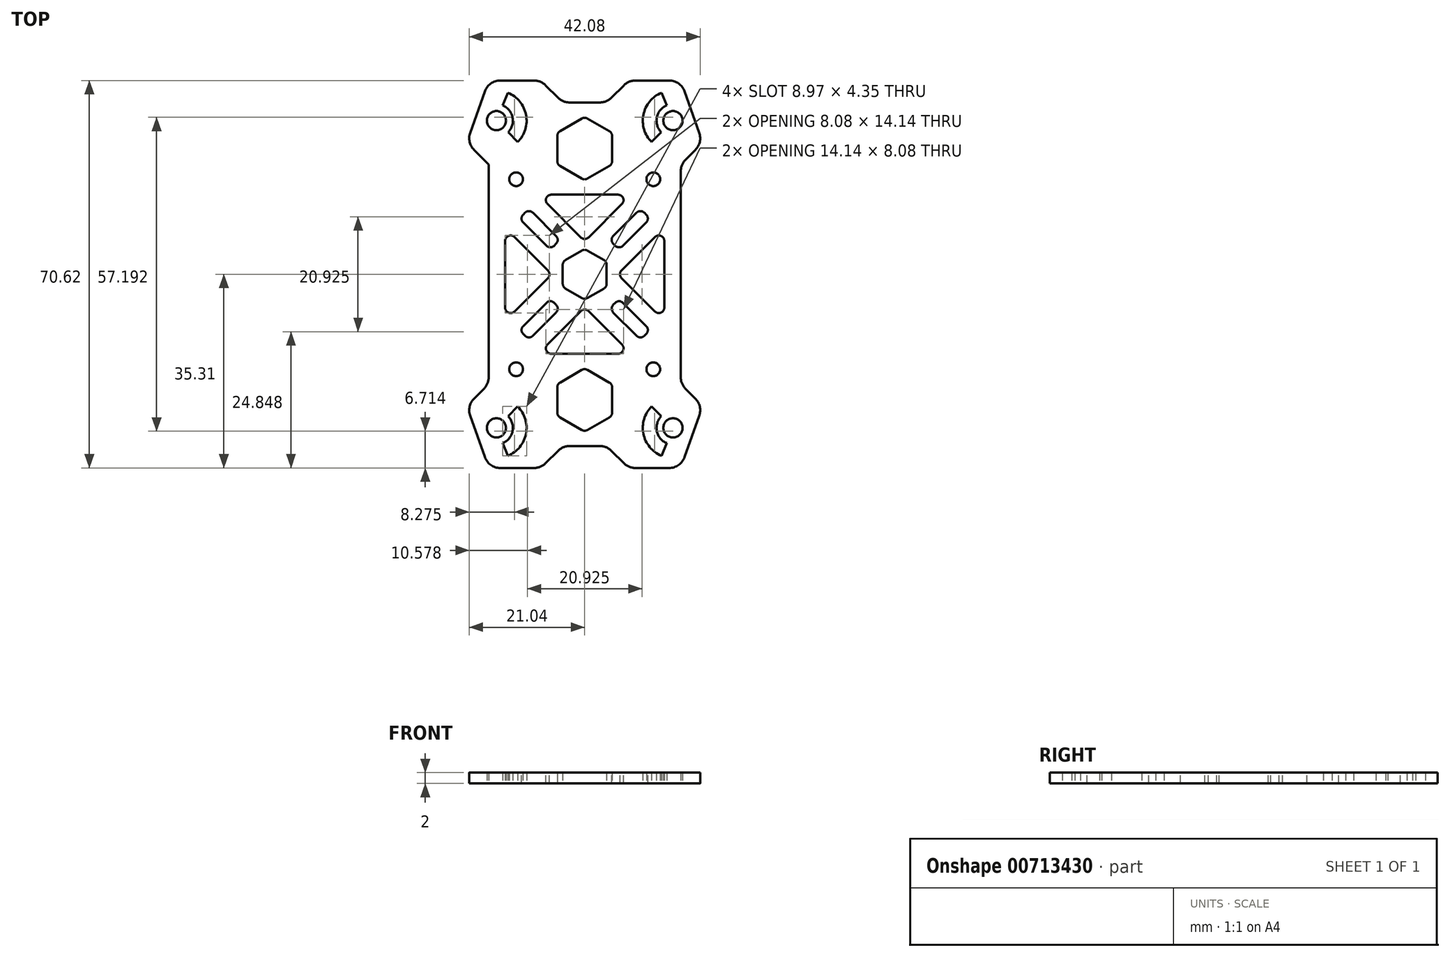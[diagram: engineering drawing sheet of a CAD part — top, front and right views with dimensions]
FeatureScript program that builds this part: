
annotation { "Feature Type Name" : "Feature", "Feature Type Description" : "" }
export const myFeature = defineFeature(function(context is Context, id is Id, definition is map)
    precondition{}
    {
        {
            var Q0;
            Q0=qCreatedBy(makeId("Top.planeOp"),FACE);
            var sketch = newSketch(context, id + "F0", { "sketchPlane" : qUnion([Q0])});
            skLineSegment(sketch, "E0.bottom", {"start": v(-10, 10) * mm, "end": v(10, 10) * mm, "construction": true});
            skLineSegment(sketch, "E0.top", {"start": v(-10, -10) * mm, "end": v(10, -10) * mm, "construction": true});
            skLineSegment(sketch, "E0.left", {"start": v(-10, 10) * mm, "end": v(-10, -10) * mm, "construction": true});
            skLineSegment(sketch, "E0.right", {"start": v(10, 10) * mm, "end": v(10, -10) * mm, "construction": true});
            skPoint(sketch, "E0.middle", {"position": v(0, 0) * mm});
            skCircle(sketch, "E1", {"center": v(-10, 10) * mm, "radius": 1.25 * mm});
            skCircle(sketch, "E2", {"center": v(10, 10) * mm, "radius": 1.25 * mm});
            skCircle(sketch, "E3", {"center": v(10, -10) * mm, "radius": 1.25 * mm});
            skCircle(sketch, "E4", {"center": v(-10, -10) * mm, "radius": 1.25 * mm});
            skLineSegment(sketch, "E5", {"start": v(-17.5, 20) * mm, "end": v(-17.5, -20) * mm});
            skLineSegment(sketch, "E6", {"start": v(-17.5, -20) * mm, "end": v(-21.5, -24) * mm});
            skLineSegment(sketch, "E7", {"start": v(-17.5, -35.31) * mm, "end": v(17.5, -35.31) * mm});
            skLineSegment(sketch, "E8", {"start": v(21.5, -24) * mm, "end": v(17.5, -20) * mm});
            skLineSegment(sketch, "E9", {"start": v(17.5, -20) * mm, "end": v(17.5, 20) * mm});
            skLineSegment(sketch, "E10", {"start": v(17.5, 20) * mm, "end": v(21.5, 24) * mm});
            skLineSegment(sketch, "E11", {"start": v(17.5, 35.31) * mm, "end": v(-17.5, 35.31) * mm});
            skLineSegment(sketch, "E12", {"start": v(-21.5, 24) * mm, "end": v(-17.5, 20) * mm});
            skLineSegment(sketch, "E13", {"start": v(-17.5, 0) * mm, "end": v(0, 0) * mm, "construction": true});
            skLineSegment(sketch, "E14", {"start": v(17.5, 0) * mm, "end": v(0, 0) * mm, "construction": true});
            skCircle(sketch, "E15", {"center": v(-16.09, 28) * mm, "radius": 1.75 * mm});
            skPoint(sketch, "E15.centerSnap0", {"position": v(-20.09, 28) * mm});
            skCircle(sketch, "E16", {"center": v(16.09, 28) * mm, "radius": 1.75 * mm});
            skPoint(sketch, "E16.centerSnap0", {"position": v(20.09, 28) * mm});
            skCircle(sketch, "E17", {"center": v(-16.09, -28) * mm, "radius": 1.75 * mm});
            skPoint(sketch, "E17.centerSnap0", {"position": v(-20.09, -28) * mm});
            skCircle(sketch, "E18", {"center": v(16.09, -28) * mm, "radius": 1.75 * mm});
            skPoint(sketch, "E18.centerSnap0", {"position": v(20.09, -28) * mm});
            skLineSegment(sketch, "E19", {"start": v(-16.09, 28) * mm, "end": v(-20.09, 28) * mm, "construction": true});
            skLineSegment(sketch, "E20", {"start": v(16.09, 28) * mm, "end": v(20.09, 28) * mm, "construction": true});
            skLineSegment(sketch, "E21", {"start": v(16.09, -28) * mm, "end": v(20.09, -28) * mm, "construction": true});
            skLineSegment(sketch, "E22", {"start": v(-16.09, -28) * mm, "end": v(-20.09, -28) * mm, "construction": true});
            skLineSegment(sketch, "E23", {"start": v(-21.5, 24) * mm, "end": v(-17.5, 35.31) * mm});
            skLineSegment(sketch, "E24", {"start": v(17.5, 35.31) * mm, "end": v(21.5, 24) * mm});
            skLineSegment(sketch, "E25", {"start": v(-17.5, -35.31) * mm, "end": v(-21.5, -24) * mm});
            skLineSegment(sketch, "E26", {"start": v(17.5, -35.31) * mm, "end": v(21.5, -24) * mm});
            skLineSegment(sketch, "E27", {"start": v(-16.09, 28) * mm, "end": v(-16.09, 20) * mm, "construction": true});
            skLineSegment(sketch, "E28", {"start": v(16.09, 20) * mm, "end": v(16.09, 28) * mm, "construction": true});
            skLineSegment(sketch, "E29", {"start": v(-16.09, -28) * mm, "end": v(-16.09, -20) * mm, "construction": true});
            skLineSegment(sketch, "E30", {"start": v(16.09, -28) * mm, "end": v(16.09, -20) * mm, "construction": true});
            skCircle(sketch, "E31.cCircle", {"center": v(0, 22.9) * mm, "radius": 5 * mm, "construction": true});
            skLineSegment(sketch, "E31.0", {"start": v(-5, 20.02) * mm, "end": v(-5, 25.8) * mm});
            skLineSegment(sketch, "E31.1", {"start": v(-5, 25.8) * mm, "end": v(0, 28.68) * mm});
            skLineSegment(sketch, "E31.2", {"start": v(0, 28.68) * mm, "end": v(5, 25.8) * mm});
            skLineSegment(sketch, "E31.3", {"start": v(5, 25.8) * mm, "end": v(5, 20.02) * mm});
            skLineSegment(sketch, "E31.4", {"start": v(5, 20.02) * mm, "end": v(0, 17.13) * mm});
            skLineSegment(sketch, "E31.5", {"start": v(0, 17.13) * mm, "end": v(-5, 20.02) * mm});
            skPoint(sketch, "E31.0.midPoint", {"position": v(-5, 22.9) * mm});
            skLineSegment(sketch, "E32", {"start": v(-11.92, 10.16) * mm, "end": v(-6.27, 4.5) * mm});
            skLineSegment(sketch, "E33", {"start": v(-6.27, 4.5) * mm, "end": v(-4.5, 6.27) * mm});
            skLineSegment(sketch, "E34", {"start": v(-4.5, 6.27) * mm, "end": v(-10.16, 11.92) * mm});
            skLineSegment(sketch, "E35", {"start": v(-10.16, 11.92) * mm, "end": v(-11.92, 10.16) * mm});
            skLineSegment(sketch, "E36.MirrorCS", {"start": v(4.5, 6.27) * mm, "end": v(10.16, 11.92) * mm});
            skLineSegment(sketch, "E37.MirrorCS", {"start": v(10.16, 11.92) * mm, "end": v(11.92, 10.16) * mm});
            skLineSegment(sketch, "E38.MirrorCS", {"start": v(11.92, 10.16) * mm, "end": v(6.27, 4.5) * mm});
            skLineSegment(sketch, "E39.MirrorCS", {"start": v(6.27, 4.5) * mm, "end": v(4.5, 6.27) * mm});
            skLineSegment(sketch, "E40.MirrorCS", {"start": v(11.92, -10.16) * mm, "end": v(6.27, -4.5) * mm});
            skLineSegment(sketch, "E41.MirrorCS", {"start": v(6.27, -4.5) * mm, "end": v(4.5, -6.27) * mm});
            skLineSegment(sketch, "E42.MirrorCS", {"start": v(4.5, -6.27) * mm, "end": v(10.16, -11.92) * mm});
            skLineSegment(sketch, "E43.MirrorCS", {"start": v(-6.27, -4.5) * mm, "end": v(-4.5, -6.27) * mm});
            skLineSegment(sketch, "E44.MirrorCS", {"start": v(-11.92, -10.16) * mm, "end": v(-6.27, -4.5) * mm});
            skLineSegment(sketch, "E45.MirrorCS", {"start": v(-4.5, -6.27) * mm, "end": v(-10.16, -11.92) * mm});
            skLineSegment(sketch, "E46.MirrorCS", {"start": v(-10.16, -11.92) * mm, "end": v(-11.92, -10.16) * mm});
            skLineSegment(sketch, "E47.MirrorCS", {"start": v(10.16, -11.92) * mm, "end": v(11.92, -10.16) * mm});
            skCircle(sketch, "E48", {"center": v(-12.5, 17.31) * mm, "radius": 1.25 * mm});
            skCircle(sketch, "E49", {"center": v(12.5, 17.31) * mm, "radius": 1.25 * mm});
            skCircle(sketch, "E50", {"center": v(-12.5, -17.31) * mm, "radius": 1.25 * mm});
            skCircle(sketch, "E51", {"center": v(12.5, -17.31) * mm, "radius": 1.25 * mm});
            skLineSegment(sketch, "E52", {"start": v(-12.5, 17.31) * mm, "end": v(-17.5, 17.31) * mm, "construction": true});
            skLineSegment(sketch, "E53", {"start": v(-12.5, 17.31) * mm, "end": v(-12.5, 35.31) * mm, "construction": true});
            skLineSegment(sketch, "E54", {"start": v(12.5, 17.31) * mm, "end": v(12.5, 35.31) * mm, "construction": true});
            skLineSegment(sketch, "E55", {"start": v(12.5, 17.31) * mm, "end": v(17.5, 17.31) * mm, "construction": true});
            skLineSegment(sketch, "E56", {"start": v(-12.5, -17.31) * mm, "end": v(-12.5, -35.31) * mm, "construction": true});
            skLineSegment(sketch, "E57", {"start": v(12.5, -17.31) * mm, "end": v(12.5, -35.31) * mm, "construction": true});
            skLineSegment(sketch, "E58", {"start": v(-12.5, -17.31) * mm, "end": v(-17.5, -17.31) * mm, "construction": true});
            skLineSegment(sketch, "E59", {"start": v(12.5, -17.31) * mm, "end": v(17.5, -17.31) * mm, "construction": true});
            skLineSegment(sketch, "E60", {"start": v(-6.01, 0) * mm, "end": v(-14.5, 8.49) * mm});
            skLineSegment(sketch, "E61", {"start": v(-14.5, 8.49) * mm, "end": v(-14.5, -8.49) * mm});
            skLineSegment(sketch, "E62", {"start": v(-14.5, -8.49) * mm, "end": v(-6.01, 0) * mm});
            skLineSegment(sketch, "E63.MirrorCS", {"start": v(6.01, 0) * mm, "end": v(14.5, 8.49) * mm});
            skLineSegment(sketch, "E64.MirrorCS", {"start": v(14.5, -8.49) * mm, "end": v(6.01, 0) * mm});
            skLineSegment(sketch, "E65.MirrorCS", {"start": v(14.5, 8.49) * mm, "end": v(14.5, -8.49) * mm});
            skLineSegment(sketch, "E66", {"start": v(-8.49, 14.5) * mm, "end": v(0, 6.01) * mm});
            skLineSegment(sketch, "E67", {"start": v(0, 6.01) * mm, "end": v(8.49, 14.5) * mm});
            skLineSegment(sketch, "E68", {"start": v(8.49, 14.5) * mm, "end": v(-8.49, 14.5) * mm});
            skLineSegment(sketch, "E69.MirrorCS", {"start": v(0, -6.01) * mm, "end": v(8.49, -14.5) * mm});
            skLineSegment(sketch, "E70.MirrorCS", {"start": v(-8.49, -14.5) * mm, "end": v(0, -6.01) * mm});
            skLineSegment(sketch, "E71.MirrorCS", {"start": v(8.49, -14.5) * mm, "end": v(-8.49, -14.5) * mm});
            skCircle(sketch, "E72.cCircle", {"center": v(0, 0) * mm, "radius": 4 * mm, "construction": true});
            skLineSegment(sketch, "E72.0", {"start": v(-4, -2.3) * mm, "end": v(-4, 2.3) * mm});
            skLineSegment(sketch, "E72.1", {"start": v(-4, 2.3) * mm, "end": v(0, 4.62) * mm});
            skLineSegment(sketch, "E72.2", {"start": v(0, 4.62) * mm, "end": v(4, 2.3) * mm});
            skLineSegment(sketch, "E72.3", {"start": v(4, 2.3) * mm, "end": v(4, -2.3) * mm});
            skLineSegment(sketch, "E72.4", {"start": v(4, -2.3) * mm, "end": v(0, -4.62) * mm});
            skLineSegment(sketch, "E72.5", {"start": v(0, -4.62) * mm, "end": v(-4, -2.3) * mm});
            skPoint(sketch, "E72.0.midPoint", {"position": v(-4, 0) * mm});
            skLineSegment(sketch, "E73.MirrorCS", {"start": v(-5, -25.8) * mm, "end": v(0, -28.68) * mm});
            skLineSegment(sketch, "E74.MirrorCS", {"start": v(0, -28.68) * mm, "end": v(5, -25.8) * mm});
            skLineSegment(sketch, "E75.MirrorCS", {"start": v(5, -20.02) * mm, "end": v(0, -17.13) * mm});
            skLineSegment(sketch, "E76.MirrorCS", {"start": v(5, -25.8) * mm, "end": v(5, -20.02) * mm});
            skLineSegment(sketch, "E77.MirrorCS", {"start": v(0, -17.13) * mm, "end": v(-5, -20.02) * mm});
            skLineSegment(sketch, "E78.MirrorCS", {"start": v(-5, -20.02) * mm, "end": v(-5, -25.8) * mm});
            skPoint(sketch, "E79.startSnap0", {"position": v(-18.09, 28) * mm});
            skLineSegment(sketch, "E80", {"start": v(-8, 35.31) * mm, "end": v(-4, 31.31) * mm});
            skLineSegment(sketch, "E81", {"start": v(-4, 31.31) * mm, "end": v(4, 31.31) * mm});
            skLineSegment(sketch, "E82", {"start": v(4, 31.31) * mm, "end": v(8, 35.31) * mm});
            skLineSegment(sketch, "E83", {"start": v(-8, 35.31) * mm, "end": v(-17.5, 35.31) * mm, "construction": true});
            skLineSegment(sketch, "E84", {"start": v(8, 35.31) * mm, "end": v(17.5, 35.31) * mm, "construction": true});
            skLineSegment(sketch, "E85.MirrorCS", {"start": v(-4, -31.31) * mm, "end": v(4, -31.31) * mm});
            skLineSegment(sketch, "E86.MirrorCS", {"start": v(-8, -35.31) * mm, "end": v(-4, -31.31) * mm});
            skLineSegment(sketch, "E87.MirrorCS", {"start": v(4, -31.31) * mm, "end": v(8, -35.31) * mm});
            skArc(sketch, "E88.converted", {"start": v(-13.96, 25.88) * mm, "mid": v(-13.14, 28.59) * mm, "end": v(-14.94, 30.77) * mm});
            skArc(sketch, "E89.converted", {"start": v(-12.2, 24.11) * mm, "mid": v(-10.7, 29.07) * mm, "end": v(-13.98, 33.08) * mm});
            skLineSegment(sketch, "E90", {"start": v(-13.96, 25.88) * mm, "end": v(-12.2, 24.11) * mm});
            skLineSegment(sketch, "E91", {"start": v(-14.94, 30.77) * mm, "end": v(-13.98, 33.08) * mm});
            skArc(sketch, "E92.MirrorCS", {"start": v(12.2, 24.11) * mm, "mid": v(10.7, 29.07) * mm, "end": v(13.98, 33.08) * mm});
            skLineSegment(sketch, "E93.MirrorCS", {"start": v(13.96, 25.88) * mm, "end": v(12.2, 24.11) * mm});
            skArc(sketch, "E94.MirrorCS", {"start": v(13.96, 25.88) * mm, "mid": v(13.14, 28.59) * mm, "end": v(14.94, 30.77) * mm});
            skLineSegment(sketch, "E95.MirrorCS", {"start": v(14.94, 30.77) * mm, "end": v(13.98, 33.08) * mm});
            skLineSegment(sketch, "E96.MirrorCS", {"start": v(14.94, -30.77) * mm, "end": v(13.98, -33.08) * mm});
            skArc(sketch, "E97.MirrorCS", {"start": v(13.96, -25.88) * mm, "mid": v(13.14, -28.59) * mm, "end": v(14.94, -30.77) * mm});
            skLineSegment(sketch, "E98.MirrorCS", {"start": v(13.96, -25.88) * mm, "end": v(12.2, -24.11) * mm});
            skArc(sketch, "E99.MirrorCS", {"start": v(12.2, -24.11) * mm, "mid": v(10.7, -29.07) * mm, "end": v(13.98, -33.08) * mm});
            skArc(sketch, "E100.MirrorCS", {"start": v(-12.2, -24.11) * mm, "mid": v(-10.7, -29.07) * mm, "end": v(-13.98, -33.08) * mm});
            skLineSegment(sketch, "E101.MirrorCS", {"start": v(-14.94, -30.77) * mm, "end": v(-13.98, -33.08) * mm});
            skArc(sketch, "E102.MirrorCS", {"start": v(-13.96, -25.88) * mm, "mid": v(-13.14, -28.59) * mm, "end": v(-14.94, -30.77) * mm});
            skLineSegment(sketch, "E103.MirrorCS", {"start": v(-13.96, -25.88) * mm, "end": v(-12.2, -24.11) * mm});
            skLineSegment(sketch, "E104", {"start": v(0, 28.68) * mm, "end": v(0, 31.31) * mm, "construction": true});
            skLineSegment(sketch, "E105", {"start": v(0, 17.13) * mm, "end": v(0, 14.5) * mm, "construction": true});
            skSolve(sketch);
        }
        {
            var Q0;
            Q0=makeQuery(id+"F0.imprint","IMPRINT",FACE,{"disambiguationData":[TD([[makeQuery(id+"F0.imprint","IMPRINT",EDGE,{"derivedFrom":sQuery(id+"F0.wireOp",EDGE,"E5")}),1.0]])]});
            extrude(context, id + "F1", {"entities" : qUnion([Q0]), "depth" : 2 * mm, "offsetDistance" : 25 * mm});
        }
        {
            var Q0;
            Q0=makeQuery(id+"F1.opExtrude","SWEPT_EDGE",EDGE,{"disambiguationData":[OSD([sQuery(id+"F0.wireOp",EDGE,"E6"),sQuery(id+"F0.wireOp",EDGE,"E25")])]});
            var Q1;
            Q1=makeQuery(id+"F1.opExtrude","SWEPT_EDGE",EDGE,{"disambiguationData":[OSD([sQuery(id+"F0.wireOp",EDGE,"E5"),sQuery(id+"F0.wireOp",EDGE,"E6")])]});
            var Q2;
            Q2=makeQuery(id+"F1.opExtrude","SWEPT_EDGE",EDGE,{"disambiguationData":[OSD([sQuery(id+"F0.wireOp",EDGE,"E7"),sQuery(id+"F0.wireOp",EDGE,"E25")])]});
            var Q3;
            Q3=makeQuery(id+"F1.opExtrude","SWEPT_EDGE",EDGE,{"disambiguationData":[OSD([sQuery(id+"F0.wireOp",EDGE,"E7"),sQuery(id+"F0.wireOp",EDGE,"E26")])]});
            var Q4;
            Q4=makeQuery(id+"F1.opExtrude","SWEPT_EDGE",EDGE,{"disambiguationData":[OSD([sQuery(id+"F0.wireOp",EDGE,"E8"),sQuery(id+"F0.wireOp",EDGE,"E26")])]});
            var Q5;
            Q5=makeQuery(id+"F1.opExtrude","SWEPT_EDGE",EDGE,{"disambiguationData":[OSD([sQuery(id+"F0.wireOp",EDGE,"E8"),sQuery(id+"F0.wireOp",EDGE,"E9")])]});
            var Q6;
            Q6=makeQuery(id+"F1.opExtrude","SWEPT_EDGE",EDGE,{"disambiguationData":[OSD([sQuery(id+"F0.wireOp",EDGE,"E9"),sQuery(id+"F0.wireOp",EDGE,"E10")])]});
            var Q7;
            Q7=makeQuery(id+"F1.opExtrude","SWEPT_EDGE",EDGE,{"disambiguationData":[OSD([sQuery(id+"F0.wireOp",EDGE,"E10"),sQuery(id+"F0.wireOp",EDGE,"E24")])]});
            var Q8;
            Q8=makeQuery(id+"F1.opExtrude","SWEPT_EDGE",EDGE,{"disambiguationData":[OSD([sQuery(id+"F0.wireOp",EDGE,"E11"),sQuery(id+"F0.wireOp",EDGE,"E24")])]});
            var Q9;
            Q9=makeQuery(id+"F1.opExtrude","SWEPT_EDGE",EDGE,{"disambiguationData":[OSD([sQuery(id+"F0.wireOp",EDGE,"E11"),sQuery(id+"F0.wireOp",EDGE,"E23")])]});
            var Q10;
            Q10=makeQuery(id+"F1.opExtrude","SWEPT_EDGE",EDGE,{"disambiguationData":[OSD([sQuery(id+"F0.wireOp",EDGE,"E12"),sQuery(id+"F0.wireOp",EDGE,"E23")])]});
            var Q11;
            Q11=makeQuery(id+"F1.opExtrude","SWEPT_EDGE",EDGE,{"disambiguationData":[OSD([sQuery(id+"F0.wireOp",EDGE,"E7"),sQuery(id+"F0.wireOp",EDGE,"E86.MirrorCS")])]});
            var Q12;
            Q12=makeQuery(id+"F1.opExtrude","SWEPT_EDGE",EDGE,{"disambiguationData":[OSD([sQuery(id+"F0.wireOp",EDGE,"E85.MirrorCS"),sQuery(id+"F0.wireOp",EDGE,"E86.MirrorCS")])]});
            var Q13;
            Q13=makeQuery(id+"F1.opExtrude","SWEPT_EDGE",EDGE,{"disambiguationData":[OSD([sQuery(id+"F0.wireOp",EDGE,"E85.MirrorCS"),sQuery(id+"F0.wireOp",EDGE,"E87.MirrorCS")])]});
            var Q14;
            Q14=makeQuery(id+"F1.opExtrude","SWEPT_EDGE",EDGE,{"disambiguationData":[OSD([sQuery(id+"F0.wireOp",EDGE,"E7"),sQuery(id+"F0.wireOp",EDGE,"E87.MirrorCS")])]});
            var Q15;
            Q15=makeQuery(id+"F1.opExtrude","SWEPT_EDGE",EDGE,{"disambiguationData":[OSD([sQuery(id+"F0.wireOp",EDGE,"E11"),sQuery(id+"F0.wireOp",EDGE,"E80")])]});
            var Q16;
            Q16=makeQuery(id+"F1.opExtrude","SWEPT_EDGE",EDGE,{"disambiguationData":[OSD([sQuery(id+"F0.wireOp",EDGE,"E80"),sQuery(id+"F0.wireOp",EDGE,"E81")])]});
            var Q17;
            Q17=makeQuery(id+"F1.opExtrude","SWEPT_EDGE",EDGE,{"disambiguationData":[OSD([sQuery(id+"F0.wireOp",EDGE,"E81"),sQuery(id+"F0.wireOp",EDGE,"E82")])]});
            var Q18;
            Q18=makeQuery(id+"F1.opExtrude","SWEPT_EDGE",EDGE,{"disambiguationData":[OSD([sQuery(id+"F0.wireOp",EDGE,"E11"),sQuery(id+"F0.wireOp",EDGE,"E82")])]});
            fillet(context, id + "F2", {"entities" : qUnion([Q0, Q1, Q2, Q3, Q4, Q5, Q6, Q7, Q8, Q9, Q10, Q11, Q12, Q13, Q14, Q15, Q16, Q17, Q18]), "radius" : 3 * mm, "tangentPropagation" : true, "allowEdgeOverflow" : false});
        }
        {
            var Q0;
            Q0=makeQuery(id+"F1.opExtrude","SWEPT_EDGE",EDGE,{"disambiguationData":[OSD([sQuery(id+"F0.wireOp",EDGE,"E34"),sQuery(id+"F0.wireOp",EDGE,"E35")])]});
            var Q1;
            Q1=makeQuery(id+"F1.opExtrude","SWEPT_EDGE",EDGE,{"disambiguationData":[OSD([sQuery(id+"F0.wireOp",EDGE,"E32"),sQuery(id+"F0.wireOp",EDGE,"E35")])]});
            var Q2;
            Q2=makeQuery(id+"F1.opExtrude","SWEPT_EDGE",EDGE,{"disambiguationData":[OSD([sQuery(id+"F0.wireOp",EDGE,"E33"),sQuery(id+"F0.wireOp",EDGE,"E34")])]});
            var Q3;
            Q3=makeQuery(id+"F1.opExtrude","SWEPT_EDGE",EDGE,{"disambiguationData":[OSD([sQuery(id+"F0.wireOp",EDGE,"E32"),sQuery(id+"F0.wireOp",EDGE,"E33")])]});
            var Q4;
            Q4=makeQuery(id+"F1.opExtrude","SWEPT_EDGE",EDGE,{"disambiguationData":[OSD([sQuery(id+"F0.wireOp",EDGE,"E36.MirrorCS"),sQuery(id+"F0.wireOp",EDGE,"E37.MirrorCS")])]});
            var Q5;
            Q5=makeQuery(id+"F1.opExtrude","SWEPT_EDGE",EDGE,{"disambiguationData":[OSD([sQuery(id+"F0.wireOp",EDGE,"E37.MirrorCS"),sQuery(id+"F0.wireOp",EDGE,"E38.MirrorCS")])]});
            var Q6;
            Q6=makeQuery(id+"F1.opExtrude","SWEPT_EDGE",EDGE,{"disambiguationData":[OSD([sQuery(id+"F0.wireOp",EDGE,"E38.MirrorCS"),sQuery(id+"F0.wireOp",EDGE,"E39.MirrorCS")])]});
            var Q7;
            Q7=makeQuery(id+"F1.opExtrude","SWEPT_EDGE",EDGE,{"disambiguationData":[OSD([sQuery(id+"F0.wireOp",EDGE,"E36.MirrorCS"),sQuery(id+"F0.wireOp",EDGE,"E39.MirrorCS")])]});
            var Q8;
            Q8=makeQuery(id+"F1.opExtrude","SWEPT_EDGE",EDGE,{"disambiguationData":[OSD([sQuery(id+"F0.wireOp",EDGE,"E44.MirrorCS"),sQuery(id+"F0.wireOp",EDGE,"E46.MirrorCS")])]});
            var Q9;
            Q9=makeQuery(id+"F1.opExtrude","SWEPT_EDGE",EDGE,{"disambiguationData":[OSD([sQuery(id+"F0.wireOp",EDGE,"E41.MirrorCS"),sQuery(id+"F0.wireOp",EDGE,"E42.MirrorCS")])]});
            var Q10;
            Q10=makeQuery(id+"F1.opExtrude","SWEPT_EDGE",EDGE,{"disambiguationData":[OSD([sQuery(id+"F0.wireOp",EDGE,"E43.MirrorCS"),sQuery(id+"F0.wireOp",EDGE,"E45.MirrorCS")])]});
            var Q11;
            Q11=makeQuery(id+"F1.opExtrude","SWEPT_EDGE",EDGE,{"disambiguationData":[OSD([sQuery(id+"F0.wireOp",EDGE,"E40.MirrorCS"),sQuery(id+"F0.wireOp",EDGE,"E47.MirrorCS")])]});
            var Q12;
            Q12=makeQuery(id+"F1.opExtrude","SWEPT_EDGE",EDGE,{"disambiguationData":[OSD([sQuery(id+"F0.wireOp",EDGE,"E42.MirrorCS"),sQuery(id+"F0.wireOp",EDGE,"E47.MirrorCS")])]});
            var Q13;
            Q13=makeQuery(id+"F1.opExtrude","SWEPT_EDGE",EDGE,{"disambiguationData":[OSD([sQuery(id+"F0.wireOp",EDGE,"E45.MirrorCS"),sQuery(id+"F0.wireOp",EDGE,"E46.MirrorCS")])]});
            var Q14;
            Q14=makeQuery(id+"F1.opExtrude","SWEPT_EDGE",EDGE,{"disambiguationData":[OSD([sQuery(id+"F0.wireOp",EDGE,"E43.MirrorCS"),sQuery(id+"F0.wireOp",EDGE,"E44.MirrorCS")])]});
            var Q15;
            Q15=makeQuery(id+"F1.opExtrude","SWEPT_EDGE",EDGE,{"disambiguationData":[OSD([sQuery(id+"F0.wireOp",EDGE,"E40.MirrorCS"),sQuery(id+"F0.wireOp",EDGE,"E41.MirrorCS")])]});
            var Q16;
            Q16=makeQuery(id+"F1.opExtrude","SWEPT_EDGE",EDGE,{"disambiguationData":[OSD([sQuery(id+"F0.wireOp",EDGE,"532293ea-ac90-4155-ae0c-07403808c71e.0"),sQuery(id+"F0.wireOp",EDGE,"532293ea-ac90-4155-ae0c-07403808c71e.5")])]});
            var Q17;
            Q17=makeQuery(id+"F1.opExtrude","SWEPT_EDGE",EDGE,{"disambiguationData":[OSD([sQuery(id+"F0.wireOp",EDGE,"532293ea-ac90-4155-ae0c-07403808c71e.4"),sQuery(id+"F0.wireOp",EDGE,"532293ea-ac90-4155-ae0c-07403808c71e.5")])]});
            var Q18;
            Q18=makeQuery(id+"F1.opExtrude","SWEPT_EDGE",EDGE,{"disambiguationData":[OSD([sQuery(id+"F0.wireOp",EDGE,"532293ea-ac90-4155-ae0c-07403808c71e.3"),sQuery(id+"F0.wireOp",EDGE,"532293ea-ac90-4155-ae0c-07403808c71e.4")])]});
            var Q19;
            Q19=makeQuery(id+"F1.opExtrude","SWEPT_EDGE",EDGE,{"disambiguationData":[OSD([sQuery(id+"F0.wireOp",EDGE,"532293ea-ac90-4155-ae0c-07403808c71e.2"),sQuery(id+"F0.wireOp",EDGE,"532293ea-ac90-4155-ae0c-07403808c71e.3")])]});
            var Q20;
            Q20=makeQuery(id+"F1.opExtrude","SWEPT_EDGE",EDGE,{"disambiguationData":[OSD([sQuery(id+"F0.wireOp",EDGE,"532293ea-ac90-4155-ae0c-07403808c71e.1"),sQuery(id+"F0.wireOp",EDGE,"532293ea-ac90-4155-ae0c-07403808c71e.2")])]});
            var Q21;
            Q21=makeQuery(id+"F1.opExtrude","SWEPT_EDGE",EDGE,{"disambiguationData":[OSD([sQuery(id+"F0.wireOp",EDGE,"532293ea-ac90-4155-ae0c-07403808c71e.0"),sQuery(id+"F0.wireOp",EDGE,"532293ea-ac90-4155-ae0c-07403808c71e.1")])]});
            var Q22;
            Q22=makeQuery(id+"F1.opExtrude","SWEPT_EDGE",EDGE,{"disambiguationData":[OSD([sQuery(id+"F0.wireOp",EDGE,"ea0782d6-4afa-4406-878f-a4188b14e591.4"),sQuery(id+"F0.wireOp",EDGE,"ea0782d6-4afa-4406-878f-a4188b14e591.5")])]});
            var Q23;
            Q23=makeQuery(id+"F1.opExtrude","SWEPT_EDGE",EDGE,{"disambiguationData":[OSD([sQuery(id+"F0.wireOp",EDGE,"ea0782d6-4afa-4406-878f-a4188b14e591.0"),sQuery(id+"F0.wireOp",EDGE,"ea0782d6-4afa-4406-878f-a4188b14e591.5")])]});
            var Q24;
            Q24=makeQuery(id+"F1.opExtrude","SWEPT_EDGE",EDGE,{"disambiguationData":[OSD([sQuery(id+"F0.wireOp",EDGE,"ea0782d6-4afa-4406-878f-a4188b14e591.0"),sQuery(id+"F0.wireOp",EDGE,"ea0782d6-4afa-4406-878f-a4188b14e591.1")])]});
            var Q25;
            Q25=makeQuery(id+"F1.opExtrude","SWEPT_EDGE",EDGE,{"disambiguationData":[OSD([sQuery(id+"F0.wireOp",EDGE,"ea0782d6-4afa-4406-878f-a4188b14e591.1"),sQuery(id+"F0.wireOp",EDGE,"ea0782d6-4afa-4406-878f-a4188b14e591.2")])]});
            var Q26;
            Q26=makeQuery(id+"F1.opExtrude","SWEPT_EDGE",EDGE,{"disambiguationData":[OSD([sQuery(id+"F0.wireOp",EDGE,"ea0782d6-4afa-4406-878f-a4188b14e591.2"),sQuery(id+"F0.wireOp",EDGE,"ea0782d6-4afa-4406-878f-a4188b14e591.3")])]});
            var Q27;
            Q27=makeQuery(id+"F1.opExtrude","SWEPT_EDGE",EDGE,{"disambiguationData":[OSD([sQuery(id+"F0.wireOp",EDGE,"ea0782d6-4afa-4406-878f-a4188b14e591.3"),sQuery(id+"F0.wireOp",EDGE,"ea0782d6-4afa-4406-878f-a4188b14e591.4")])]});
            var Q28;
            Q28=makeQuery(id+"F1.opExtrude","SWEPT_EDGE",EDGE,{"disambiguationData":[OSD([sQuery(id+"F0.wireOp",EDGE,"E31.3"),sQuery(id+"F0.wireOp",EDGE,"E31.4")])]});
            var Q29;
            Q29=makeQuery(id+"F1.opExtrude","SWEPT_EDGE",EDGE,{"disambiguationData":[OSD([sQuery(id+"F0.wireOp",EDGE,"E31.2"),sQuery(id+"F0.wireOp",EDGE,"E31.3")])]});
            var Q30;
            Q30=makeQuery(id+"F1.opExtrude","SWEPT_EDGE",EDGE,{"disambiguationData":[OSD([sQuery(id+"F0.wireOp",EDGE,"E31.1"),sQuery(id+"F0.wireOp",EDGE,"E31.2")])]});
            var Q31;
            Q31=makeQuery(id+"F1.opExtrude","SWEPT_EDGE",EDGE,{"disambiguationData":[OSD([sQuery(id+"F0.wireOp",EDGE,"E31.0"),sQuery(id+"F0.wireOp",EDGE,"E31.1")])]});
            var Q32;
            Q32=makeQuery(id+"F1.opExtrude","SWEPT_EDGE",EDGE,{"disambiguationData":[OSD([sQuery(id+"F0.wireOp",EDGE,"E31.0"),sQuery(id+"F0.wireOp",EDGE,"E31.5")])]});
            var Q33;
            Q33=makeQuery(id+"F1.opExtrude","SWEPT_EDGE",EDGE,{"disambiguationData":[OSD([sQuery(id+"F0.wireOp",EDGE,"E31.4"),sQuery(id+"F0.wireOp",EDGE,"E31.5")])]});
            var Q34;
            Q34=makeQuery(id+"F1.opExtrude","SWEPT_EDGE",EDGE,{"disambiguationData":[OSD([sQuery(id+"F0.wireOp",EDGE,"E69.MirrorCS"),sQuery(id+"F0.wireOp",EDGE,"E71.MirrorCS")])]});
            var Q35;
            Q35=makeQuery(id+"F1.opExtrude","SWEPT_EDGE",EDGE,{"disambiguationData":[OSD([sQuery(id+"F0.wireOp",EDGE,"E70.MirrorCS"),sQuery(id+"F0.wireOp",EDGE,"E71.MirrorCS")])]});
            var Q36;
            Q36=makeQuery(id+"F1.opExtrude","SWEPT_EDGE",EDGE,{"disambiguationData":[OSD([sQuery(id+"F0.wireOp",EDGE,"E69.MirrorCS"),sQuery(id+"F0.wireOp",EDGE,"E70.MirrorCS")])]});
            var Q37;
            Q37=makeQuery(id+"F1.opExtrude","SWEPT_EDGE",EDGE,{"disambiguationData":[OSD([sQuery(id+"F0.wireOp",EDGE,"E66"),sQuery(id+"F0.wireOp",EDGE,"E67")])]});
            var Q38;
            Q38=makeQuery(id+"F1.opExtrude","SWEPT_EDGE",EDGE,{"disambiguationData":[OSD([sQuery(id+"F0.wireOp",EDGE,"E67"),sQuery(id+"F0.wireOp",EDGE,"E68")])]});
            var Q39;
            Q39=makeQuery(id+"F1.opExtrude","SWEPT_EDGE",EDGE,{"disambiguationData":[OSD([sQuery(id+"F0.wireOp",EDGE,"E66"),sQuery(id+"F0.wireOp",EDGE,"E68")])]});
            var Q40;
            Q40=makeQuery(id+"F1.opExtrude","SWEPT_EDGE",EDGE,{"disambiguationData":[OSD([sQuery(id+"F0.wireOp",EDGE,"E60"),sQuery(id+"F0.wireOp",EDGE,"E62")])]});
            var Q41;
            Q41=makeQuery(id+"F1.opExtrude","SWEPT_EDGE",EDGE,{"disambiguationData":[OSD([sQuery(id+"F0.wireOp",EDGE,"E60"),sQuery(id+"F0.wireOp",EDGE,"E61")])]});
            var Q42;
            Q42=makeQuery(id+"F1.opExtrude","SWEPT_EDGE",EDGE,{"disambiguationData":[OSD([sQuery(id+"F0.wireOp",EDGE,"E61"),sQuery(id+"F0.wireOp",EDGE,"E62")])]});
            var Q43;
            Q43=makeQuery(id+"F1.opExtrude","SWEPT_EDGE",EDGE,{"disambiguationData":[OSD([sQuery(id+"F0.wireOp",EDGE,"E63.MirrorCS"),sQuery(id+"F0.wireOp",EDGE,"E65.MirrorCS")])]});
            var Q44;
            Q44=makeQuery(id+"F1.opExtrude","SWEPT_EDGE",EDGE,{"disambiguationData":[OSD([sQuery(id+"F0.wireOp",EDGE,"E63.MirrorCS"),sQuery(id+"F0.wireOp",EDGE,"E64.MirrorCS")])]});
            var Q45;
            Q45=makeQuery(id+"F1.opExtrude","SWEPT_EDGE",EDGE,{"disambiguationData":[OSD([sQuery(id+"F0.wireOp",EDGE,"E64.MirrorCS"),sQuery(id+"F0.wireOp",EDGE,"E65.MirrorCS")])]});
            var Q46;
            Q46=makeQuery(id+"F1.opExtrude","SWEPT_EDGE",EDGE,{"disambiguationData":[OSD([sQuery(id+"F0.wireOp",EDGE,"E77.MirrorCS"),sQuery(id+"F0.wireOp",EDGE,"E78.MirrorCS")])]});
            var Q47;
            Q47=makeQuery(id+"F1.opExtrude","SWEPT_EDGE",EDGE,{"disambiguationData":[OSD([sQuery(id+"F0.wireOp",EDGE,"E75.MirrorCS"),sQuery(id+"F0.wireOp",EDGE,"E77.MirrorCS")])]});
            var Q48;
            Q48=makeQuery(id+"F1.opExtrude","SWEPT_EDGE",EDGE,{"disambiguationData":[OSD([sQuery(id+"F0.wireOp",EDGE,"E75.MirrorCS"),sQuery(id+"F0.wireOp",EDGE,"E76.MirrorCS")])]});
            var Q49;
            Q49=makeQuery(id+"F1.opExtrude","SWEPT_EDGE",EDGE,{"disambiguationData":[OSD([sQuery(id+"F0.wireOp",EDGE,"E74.MirrorCS"),sQuery(id+"F0.wireOp",EDGE,"E76.MirrorCS")])]});
            var Q50;
            Q50=makeQuery(id+"F1.opExtrude","SWEPT_EDGE",EDGE,{"disambiguationData":[OSD([sQuery(id+"F0.wireOp",EDGE,"E73.MirrorCS"),sQuery(id+"F0.wireOp",EDGE,"E74.MirrorCS")])]});
            var Q51;
            Q51=makeQuery(id+"F1.opExtrude","SWEPT_EDGE",EDGE,{"disambiguationData":[OSD([sQuery(id+"F0.wireOp",EDGE,"E73.MirrorCS"),sQuery(id+"F0.wireOp",EDGE,"E78.MirrorCS")])]});
            var Q52;
            Q52=makeQuery(id+"F1.opExtrude","SWEPT_EDGE",EDGE,{"disambiguationData":[OSD([sQuery(id+"F0.wireOp",EDGE,"E72.2"),sQuery(id+"F0.wireOp",EDGE,"E72.3")])]});
            var Q53;
            Q53=makeQuery(id+"F1.opExtrude","SWEPT_EDGE",EDGE,{"disambiguationData":[OSD([sQuery(id+"F0.wireOp",EDGE,"E72.3"),sQuery(id+"F0.wireOp",EDGE,"E72.4")])]});
            var Q54;
            Q54=makeQuery(id+"F1.opExtrude","SWEPT_EDGE",EDGE,{"disambiguationData":[OSD([sQuery(id+"F0.wireOp",EDGE,"E72.4"),sQuery(id+"F0.wireOp",EDGE,"E72.5")])]});
            var Q55;
            Q55=makeQuery(id+"F1.opExtrude","SWEPT_EDGE",EDGE,{"disambiguationData":[OSD([sQuery(id+"F0.wireOp",EDGE,"E72.0"),sQuery(id+"F0.wireOp",EDGE,"E72.5")])]});
            var Q56;
            Q56=makeQuery(id+"F1.opExtrude","SWEPT_EDGE",EDGE,{"disambiguationData":[OSD([sQuery(id+"F0.wireOp",EDGE,"E72.0"),sQuery(id+"F0.wireOp",EDGE,"E72.1")])]});
            var Q57;
            Q57=makeQuery(id+"F1.opExtrude","SWEPT_EDGE",EDGE,{"disambiguationData":[OSD([sQuery(id+"F0.wireOp",EDGE,"E72.1"),sQuery(id+"F0.wireOp",EDGE,"E72.2")])]});
            var Q58;
            Q58=makeQuery(id+"F1.opExtrude","SWEPT_EDGE",EDGE,{"disambiguationData":[OSD([sQuery(id+"F0.wireOp",EDGE,"jIcQtBkd-RNAK-voPD-VDb6-8c8M7gbZZoD9"),sQuery(id+"F0.wireOp",EDGE,"DpfN9RD4-MQtL-8Lwk-hxLt-LieSIOUlTDS9")])]});
            var Q59;
            Q59=makeQuery(id+"F1.opExtrude","SWEPT_EDGE",EDGE,{"disambiguationData":[OSD([sQuery(id+"F0.wireOp",EDGE,"jIcQtBkd-RNAK-voPD-VDb6-8c8M7gbZZoD9"),sQuery(id+"F0.wireOp",EDGE,"E79")])]});
            var Q60;
            Q60=makeQuery(id+"F1.opExtrude","SWEPT_EDGE",EDGE,{"disambiguationData":[OSD([sQuery(id+"F0.wireOp",EDGE,"3df85af8-d721-45ed-88db-ec41ec0f3f6a.0"),sQuery(id+"F0.wireOp",EDGE,"E79")])]});
            var Q61;
            Q61=makeQuery(id+"F1.opExtrude","SWEPT_EDGE",EDGE,{"disambiguationData":[OSD([sQuery(id+"F0.wireOp",EDGE,"3df85af8-d721-45ed-88db-ec41ec0f3f6a.0"),sQuery(id+"F0.wireOp",EDGE,"DpfN9RD4-MQtL-8Lwk-hxLt-LieSIOUlTDS9")])]});
            var Q62;
            Q62=makeQuery(id+"F1.opExtrude","SWEPT_EDGE",EDGE,{"disambiguationData":[OSD([sQuery(id+"F0.wireOp",EDGE,"88661b05-4e5b-41a5-9158-386284e9b28d0.MirrorCS"),sQuery(id+"F0.wireOp",EDGE,"baf3c9ff-ed3c-4cd9-9009-9f0cfddc39c10.MirrorCS")])]});
            var Q63;
            Q63=makeQuery(id+"F1.opExtrude","SWEPT_EDGE",EDGE,{"disambiguationData":[OSD([sQuery(id+"F0.wireOp",EDGE,"acfb2029-cb6e-4764-b986-3aaf6efb55680.MirrorCS"),sQuery(id+"F0.wireOp",EDGE,"88661b05-4e5b-41a5-9158-386284e9b28d0.MirrorCS")])]});
            var Q64;
            Q64=makeQuery(id+"F1.opExtrude","SWEPT_EDGE",EDGE,{"disambiguationData":[OSD([sQuery(id+"F0.wireOp",EDGE,"acfb2029-cb6e-4764-b986-3aaf6efb55680.MirrorCS"),sQuery(id+"F0.wireOp",EDGE,"821cb638-665d-4bed-a857-1df426e795470.MirrorCS")])]});
            var Q65;
            Q65=makeQuery(id+"F1.opExtrude","SWEPT_EDGE",EDGE,{"disambiguationData":[OSD([sQuery(id+"F0.wireOp",EDGE,"baf3c9ff-ed3c-4cd9-9009-9f0cfddc39c10.MirrorCS"),sQuery(id+"F0.wireOp",EDGE,"821cb638-665d-4bed-a857-1df426e795470.MirrorCS")])]});
            var Q66;
            Q66=makeQuery(id+"F1.opExtrude","SWEPT_EDGE",EDGE,{"disambiguationData":[OSD([sQuery(id+"F0.wireOp",EDGE,"45fffaef-67e4-4282-a54b-d6372ed412fb0.MirrorCS"),sQuery(id+"F0.wireOp",EDGE,"e5fde58e-1f1f-4593-bf8c-39d572505fff0.MirrorCS")])]});
            var Q67;
            Q67=makeQuery(id+"F1.opExtrude","SWEPT_EDGE",EDGE,{"disambiguationData":[OSD([sQuery(id+"F0.wireOp",EDGE,"5abd73af-9055-4aa5-be6a-64f9c15c41c10.MirrorCS"),sQuery(id+"F0.wireOp",EDGE,"e5fde58e-1f1f-4593-bf8c-39d572505fff0.MirrorCS")])]});
            var Q68;
            Q68=makeQuery(id+"F1.opExtrude","SWEPT_EDGE",EDGE,{"disambiguationData":[OSD([sQuery(id+"F0.wireOp",EDGE,"45fffaef-67e4-4282-a54b-d6372ed412fb0.MirrorCS"),sQuery(id+"F0.wireOp",EDGE,"04f341b0-4908-46cd-9700-0e3d8dce83bb0.MirrorCS")])]});
            var Q69;
            Q69=makeQuery(id+"F1.opExtrude","SWEPT_EDGE",EDGE,{"disambiguationData":[OSD([sQuery(id+"F0.wireOp",EDGE,"5abd73af-9055-4aa5-be6a-64f9c15c41c10.MirrorCS"),sQuery(id+"F0.wireOp",EDGE,"04f341b0-4908-46cd-9700-0e3d8dce83bb0.MirrorCS")])]});
            var Q70;
            Q70=makeQuery(id+"F1.opExtrude","SWEPT_EDGE",EDGE,{"disambiguationData":[OSD([sQuery(id+"F0.wireOp",EDGE,"8fb2201b-9011-4cad-994a-62a85c7c84110.MirrorCS"),sQuery(id+"F0.wireOp",EDGE,"7c2e7590-9ec6-45c2-a70c-3f51167bab4d0.MirrorCS")])]});
            var Q71;
            Q71=makeQuery(id+"F1.opExtrude","SWEPT_EDGE",EDGE,{"disambiguationData":[OSD([sQuery(id+"F0.wireOp",EDGE,"8fb2201b-9011-4cad-994a-62a85c7c84110.MirrorCS"),sQuery(id+"F0.wireOp",EDGE,"2ee6ce83-d7db-4430-a296-fdb23fabccdf0.MirrorCS")])]});
            var Q72;
            Q72=makeQuery(id+"F1.opExtrude","SWEPT_EDGE",EDGE,{"disambiguationData":[OSD([sQuery(id+"F0.wireOp",EDGE,"f89f995f-ac8a-4c00-b812-9b9d41a8bd130.MirrorCS"),sQuery(id+"F0.wireOp",EDGE,"2ee6ce83-d7db-4430-a296-fdb23fabccdf0.MirrorCS")])]});
            var Q73;
            Q73=makeQuery(id+"F1.opExtrude","SWEPT_EDGE",EDGE,{"disambiguationData":[OSD([sQuery(id+"F0.wireOp",EDGE,"7c2e7590-9ec6-45c2-a70c-3f51167bab4d0.MirrorCS"),sQuery(id+"F0.wireOp",EDGE,"f89f995f-ac8a-4c00-b812-9b9d41a8bd130.MirrorCS")])]});
            fillet(context, id + "F3", {"entities" : qUnion([Q0, Q1, Q2, Q3, Q4, Q5, Q6, Q7, Q8, Q9, Q10, Q11, Q12, Q13, Q14, Q15, Q16, Q17, Q18, Q19, Q20, Q21, Q22, Q23, Q24, Q25, Q26, Q27, Q28, Q29, Q30, Q31, Q32, Q33, Q34, Q35, Q36, Q37, Q38, Q39, Q40, Q41, Q42, Q43, Q44, Q45, Q46, Q47, Q48, Q49, Q50, Q51, Q52, Q53, Q54, Q55, Q56, Q57, Q58, Q59, Q60, Q61, Q62, Q63, Q64, Q65, Q66, Q67, Q68, Q69, Q70, Q71, Q72, Q73]), "radius" : 1 * mm, "tangentPropagation" : true, "allowEdgeOverflow" : false});
        }
    });
